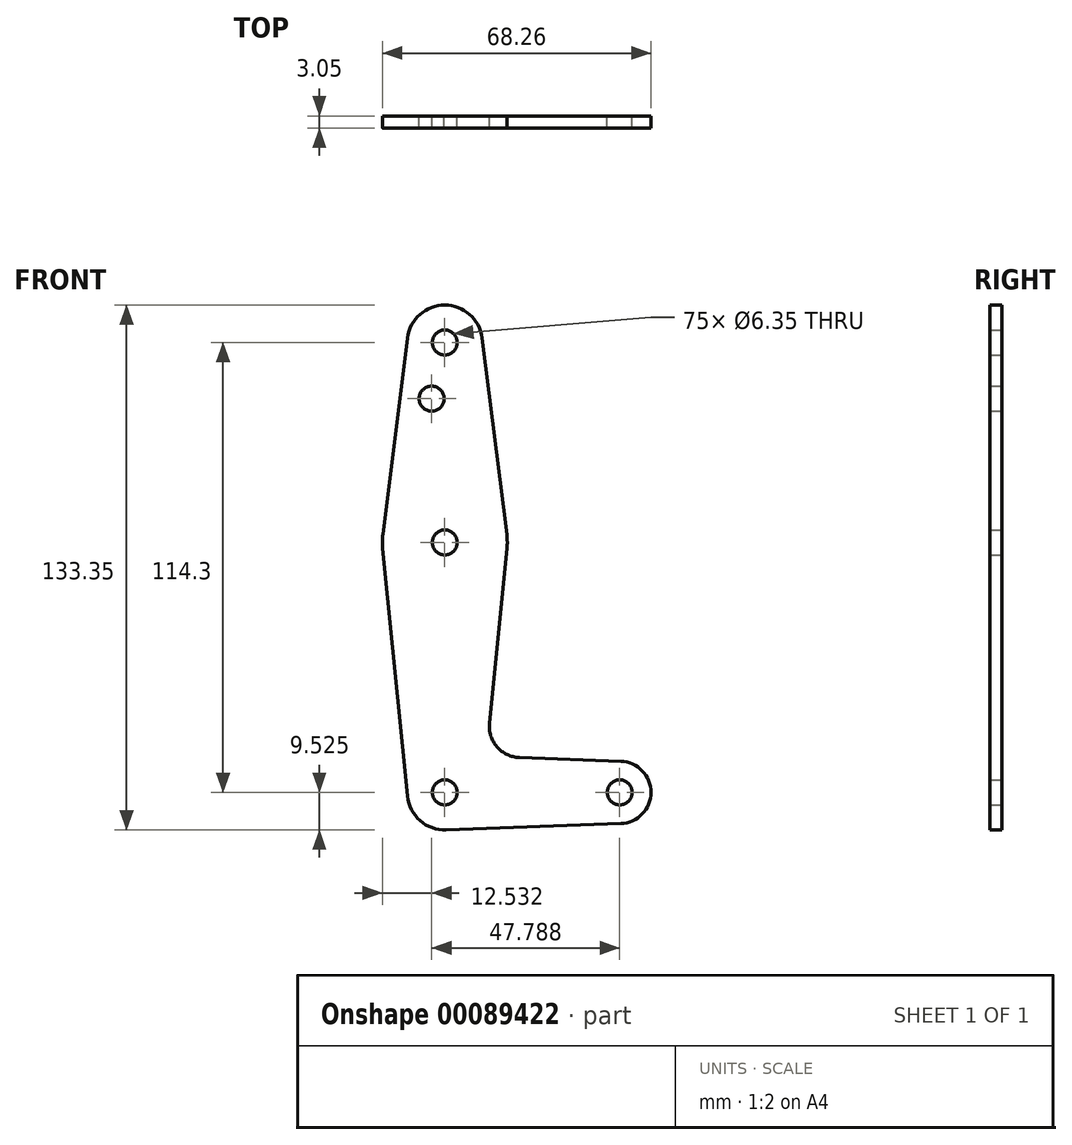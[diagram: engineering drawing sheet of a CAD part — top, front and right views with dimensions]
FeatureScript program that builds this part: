
annotation { "Feature Type Name" : "Feature", "Feature Type Description" : "" }
export const myFeature = defineFeature(function(context is Context, id is Id, definition is map)
    precondition{}
    {
        {
            var Q0;
            Q0=qCreatedBy(makeId("Front.planeOp"),FACE);
            var sketch = newSketch(context, id + "F0", { "sketchPlane" : qUnion([Q0])});
            skLineSegment(sketch, "E0", {"start": v(0, 58.73) * mm, "end": v(0, -55.57) * mm, "construction": true});
            skLineSegment(sketch, "E1", {"start": v(0, -55.57) * mm, "end": v(44.45, -55.57) * mm, "construction": true});
            skCircle(sketch, "E2", {"center": v(0, -55.57) * mm, "radius": 9.53 * mm});
            skCircle(sketch, "E3", {"center": v(0, 7.93) * mm, "radius": 15.88 * mm});
            skCircle(sketch, "E4", {"center": v(0, 58.73) * mm, "radius": 9.53 * mm});
            skCircle(sketch, "E5", {"center": v(44.45, -55.57) * mm, "radius": 7.94 * mm});
            skCircle(sketch, "E6", {"center": v(0, 58.73) * mm, "radius": 3.18 * mm});
            skCircle(sketch, "E7", {"center": v(-3.34, 44.46) * mm, "radius": 3.18 * mm});
            skCircle(sketch, "E8", {"center": v(0, 7.93) * mm, "radius": 3.18 * mm});
            skCircle(sketch, "E9", {"center": v(0, -55.57) * mm, "radius": 3.18 * mm});
            skCircle(sketch, "E10", {"center": v(44.45, -55.57) * mm, "radius": 3.18 * mm});
            skLineSegment(sketch, "E11", {"start": v(-9.45, 59.93) * mm, "end": v(-15.75, 9.92) * mm});
            skLineSegment(sketch, "E12", {"start": v(9.45, 59.93) * mm, "end": v(15.75, 9.92) * mm});
            skLineSegment(sketch, "E13", {"start": v(-15.8, 6.35) * mm, "end": v(-9.48, -56.52) * mm});
            skLineSegment(sketch, "E14", {"start": v(11.34, -37.97) * mm, "end": v(15.8, 6.35) * mm});
            skLineSegment(sketch, "E15", {"start": v(18.97, -46.71) * mm, "end": v(44.73, -47.63) * mm});
            skLineSegment(sketch, "E16", {"start": v(0.34, -65.08) * mm, "end": v(44.73, -63.5) * mm});
            skArc(sketch, "E17.filletArc", {"start": v(11.34, -37.97) * mm, "mid": v(13.26, -44) * mm, "end": v(18.97, -46.71) * mm});
            skSolve(sketch);
        }
        {
            var Q0;
            Q0 = qSketchRegion(id + "F0", true);
            extrude(context, id + "F1", {"entities" : qUnion([Q0]), "depth" : 3.05 * mm});
        }
    });
